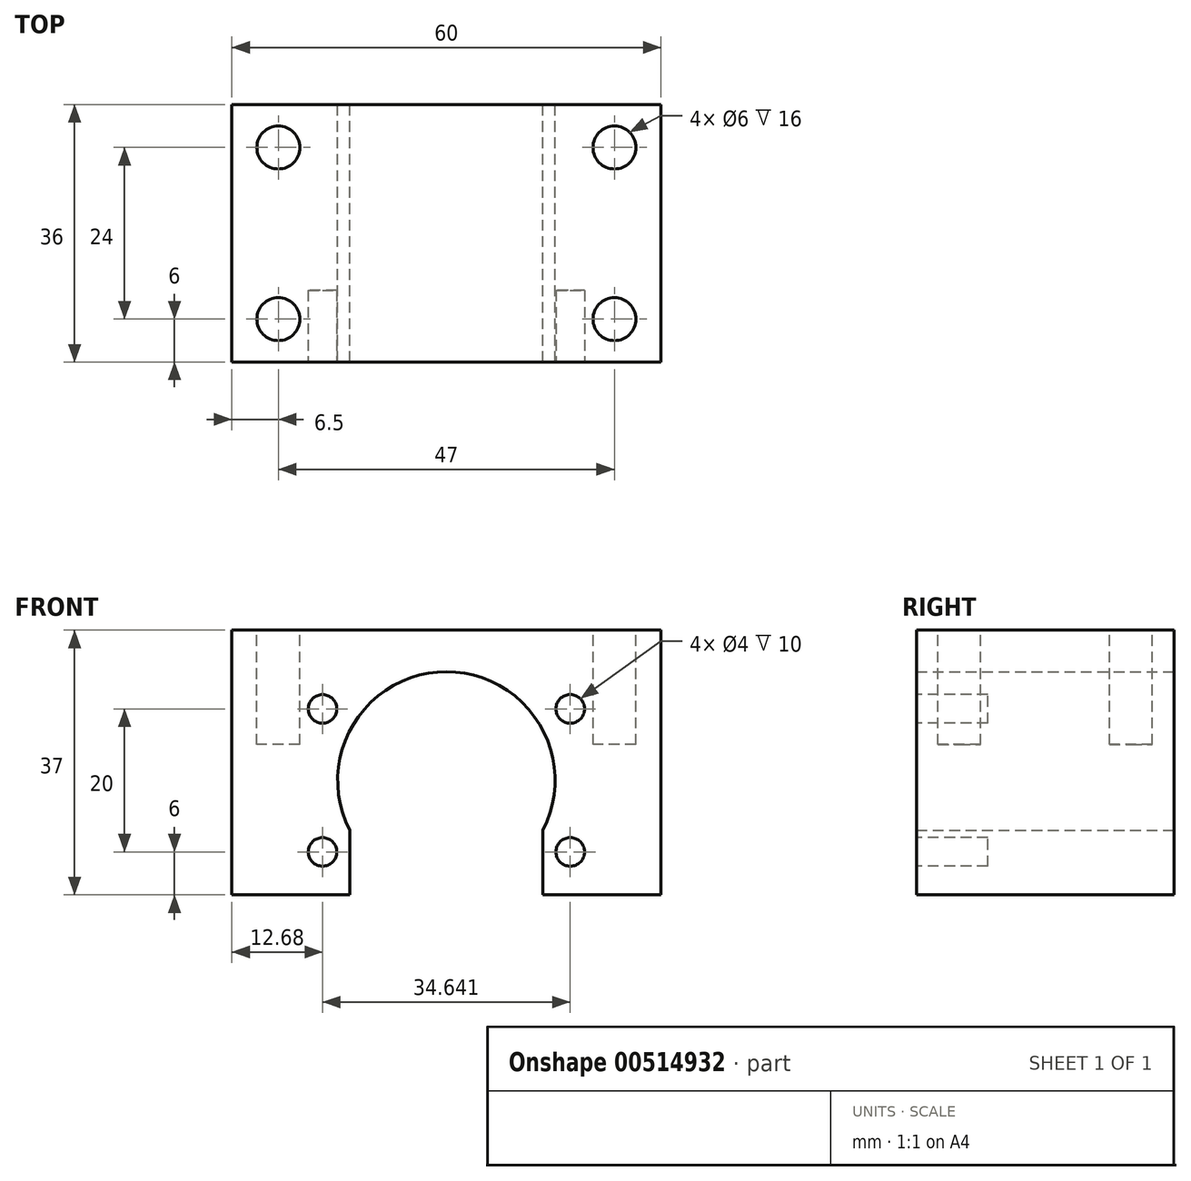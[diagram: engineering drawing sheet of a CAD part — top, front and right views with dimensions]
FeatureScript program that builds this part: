
annotation { "Feature Type Name" : "Feature", "Feature Type Description" : "" }
export const myFeature = defineFeature(function(context is Context, id is Id, definition is map)
    precondition{}
    {
        {
            var Q0;
            Q0=qCreatedBy(makeId("Front.planeOp"),FACE);
            var sketch = newSketch(context, id + "F0", { "sketchPlane" : qUnion([Q0])});
            skArc(sketch, "E0", {"start": v(13.5, -6.98) * mm, "mid": v(0, 15.2) * mm, "end": v(-13.5, -6.98) * mm});
            skLineSegment(sketch, "E1.bottom", {"start": v(-30, 21) * mm, "end": v(30, 21) * mm});
            skLineSegment(sketch, "E1.top", {"start": v(-30, -16) * mm, "end": v(-13.5, -16) * mm});
            skLineSegment(sketch, "E1.left", {"start": v(-30, 21) * mm, "end": v(-30, -16) * mm});
            skLineSegment(sketch, "E1.right", {"start": v(30, 21) * mm, "end": v(30, -16) * mm});
            skLineSegment(sketch, "E2", {"start": v(13.5, -16) * mm, "end": v(13.5, -6.98) * mm});
            skLineSegment(sketch, "E3", {"start": v(-13.5, -16) * mm, "end": v(-13.5, -6.98) * mm});
            skLineSegment(sketch, "E4.trimOffspring", {"start": v(13.5, -16) * mm, "end": v(30, -16) * mm});
            skSolve(sketch);
        }
        {
            var Q0;
            Q0=makeQuery(id+"F0.imprint","IMPRINT",FACE,{"disambiguationData":[TD([[makeQuery(id+"F0.imprint","IMPRINT",EDGE,{"derivedFrom":sQuery(id+"F0.wireOp",EDGE,"E0")}),-1.0]])]});
            extrude(context, id + "F1", {"entities" : qUnion([Q0]), "endBound" : BoundingType.SYMMETRIC, "depth" : 36 * mm, "offsetDistance" : 25 * mm});
        }
        {
            var Q0;
            Q0=makeQuery(id+"F1.opExtrude","CAP_FACE",FACE,{"disambiguationData":[OSD([sQuery(id+"F0.wireOp",EDGE,"E0"),sQuery(id+"F0.wireOp",EDGE,"E1.bottom"),sQuery(id+"F0.wireOp",EDGE,"E1.top"),sQuery(id+"F0.wireOp",EDGE,"E1.left"),sQuery(id+"F0.wireOp",EDGE,"E1.right"),sQuery(id+"F0.wireOp",EDGE,"E2"),sQuery(id+"F0.wireOp",EDGE,"E3"),sQuery(id+"F0.wireOp",EDGE,"E4.trimOffspring")])],"isStart":false});
            var sketch = newSketch(context, id + "F2", { "sketchPlane" : qUnion([Q0])});
            skPoint(sketch, "E5", {"position": v(-17.32, -10) * mm});
            skPoint(sketch, "E6", {"position": v(-17.32, 10) * mm});
            skPoint(sketch, "E7", {"position": v(17.32, 10) * mm});
            skPoint(sketch, "E8", {"position": v(17.32, -10) * mm});
            skLineSegment(sketch, "E9", {"start": v(0, 0) * mm, "end": v(-17.32, 10) * mm, "construction": true});
            skLineSegment(sketch, "E10", {"start": v(0, 0) * mm, "end": v(-17.32, -10) * mm, "construction": true});
            skCircle(sketch, "E11", {"center": v(-17.32, 10) * mm, "radius": 2 * mm});
            skCircle(sketch, "E12", {"center": v(17.32, 10) * mm, "radius": 2 * mm});
            skCircle(sketch, "E13", {"center": v(17.32, -10) * mm, "radius": 2 * mm});
            skCircle(sketch, "E14", {"center": v(-17.32, -10) * mm, "radius": 2 * mm});
            skSolve(sketch);
        }
        {
            var Q0;
            Q0=makeQuery(id+"F1.opExtrude","SWEPT_FACE",FACE,{"disambiguationData":[OSD([sQuery(id+"F0.wireOp",EDGE,"E1.bottom")])]});
            var sketch = newSketch(context, id + "F3", { "sketchPlane" : qUnion([Q0])});
            skPoint(sketch, "E15", {"position": v(-23.5, 12) * mm});
            skPoint(sketch, "E16", {"position": v(-23.5, -12) * mm});
            skPoint(sketch, "E17", {"position": v(23.5, -12) * mm});
            skPoint(sketch, "E18", {"position": v(23.5, 12) * mm});
            skCircle(sketch, "E19", {"center": v(-23.5, 12) * mm, "radius": 3 * mm});
            skCircle(sketch, "E20", {"center": v(23.5, 12) * mm, "radius": 3 * mm});
            skCircle(sketch, "E21", {"center": v(23.5, -12) * mm, "radius": 3 * mm});
            skCircle(sketch, "E22", {"center": v(-23.5, -12) * mm, "radius": 3 * mm});
            skSolve(sketch);
        }
        {
            var Q0;
            Q0 = qSketchRegion(id + "F2", true);
            extrude(context, id + "F4", {"entities" : qUnion([Q0]), "operationType" : NewBodyOperationType.REMOVE, "oppositeDirection" : true, "depth" : 10 * mm, "offsetDistance" : 25 * mm});
        }
        {
            var Q0;
            Q0 = qSketchRegion(id + "F3", true);
            extrude(context, id + "F5", {"entities" : qUnion([Q0]), "operationType" : NewBodyOperationType.REMOVE, "oppositeDirection" : true, "depth" : 16 * mm, "offsetDistance" : 25 * mm});
        }
    });
